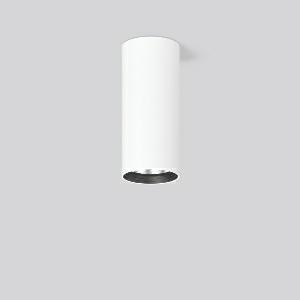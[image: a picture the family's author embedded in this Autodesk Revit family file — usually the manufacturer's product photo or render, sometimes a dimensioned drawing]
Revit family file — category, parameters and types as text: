
# Revit family: heledon_mini_a_931200_002_2_76_6b54
name_source: partatom
category: Lighting Fixtures
units: mm (PartAtom-declared; Revit-internal decimal feet)

## family parameters
Cut with Voids When Loaded = No
Host = Face
Light Source = No
Part Type = Normal
Room Calculation Point = No
Round Connector Dimension = Use Diameter
Shared = No

## types (1)
- HELEDON mini A (1 x LED Modul 927, 2400 lm, 2700)
    Apparent Load = 20 VA
    Approval mark = CE
    CIE Flux Codes = 100 100 100 100 100
    Color Rendering = 92
    Color Temperature = 2700
    Default Elevation = 1800 mm
    Description = Series: HELEDON mini
Cylindrical surface-mounted downlight. Housing: die-cast aluminium, powder-coated. Internal ceiling frame polycarbonate with bayonet mounting. Black plastic ring and recessed LED to prevent glare from the side. Optical assembly with reflector made of MIRO-Silver with 98% total light reflection for outstanding efficiency - can be changed without tools. Best colour rendering index Ra>90. Suitable for Ceiling mounting. Easy installation with a separate ceiling frame with bayonet mounting and plug connection. Driver integrated. Connected via plug-in connector. High quality converter without flickering and stroboscopic effect. The following accessories can be mounted without use of tools: interchangeable lenses, decorative glasses, honeycomb louvre, clear and frosted diffusers, white interchangeable plastic ring. 
Colour: traffic white, matt (RAL 9016)
Diameter: 87 mm
Height: 197 mm
Lamp: LED
Socket: without socket
Colour temperature: 2700K
Colour rendering index (CRI): 92
System power: 20 W
Rated luminous flux: 2400 lm
Luminous efficiency: 120 lm/W
Control gear: Converter, dimmable, DALI
Protection class: I
Type of protection: IP 20
    Height = 197 mm
    Lamp = 1 x LED Modul 927
    Lamp Light Flux = 2400 lm
    Lamp count = 1
    Length = 87 mm
    Lifetime = 50000 h
    Luminous efficacy = 120 lm/W
    Manufacturer = RZB
    ModVariant = No
    Model = 931200.002.2.76
    Mounting Place = Ceiling
    Mounting Type = Surface mounted
    Number of Poles = 1
    OnlyDefault = Yes
    Power Factor = 1
    Product Name = HELEDON mini A
    Product group = Surface mounted downlights
    ProductGroupID = 302
    Protection Class = Protection class I
    Protection Degree = IP 20
    RLX_Detail_Level = 1
    RLX_Emergency_Light_Flux = 0 lm
    RLX_Emergency_Type = 0
    RLX_Emergency_Type_DB = No
    RlxData = <blob elided: 106821 chars, md5=5267f95a>
    Socket = socket
    Standby Power = 0 W
    System Light Flux = 2400 lm
    System Power = 20 W
    Type Comments = Product without accessories
    Type Image = 931188.002.jpg
    URL = http://relux.com
    VarID = ---
    Voltage = 230 V
    Voltage Range = 220-240 V
    Weight = 0.00 kg
    Width = 0 mm  [stored 0 ft]

note: [stored X ft] marks values corroborated as IEEE doubles in the binary element streams (Revit-internal decimal feet)

## geometry (parser evidence)
native form markers: Blend x4, Sweep x11
no freeform markers — native parametric forms only
